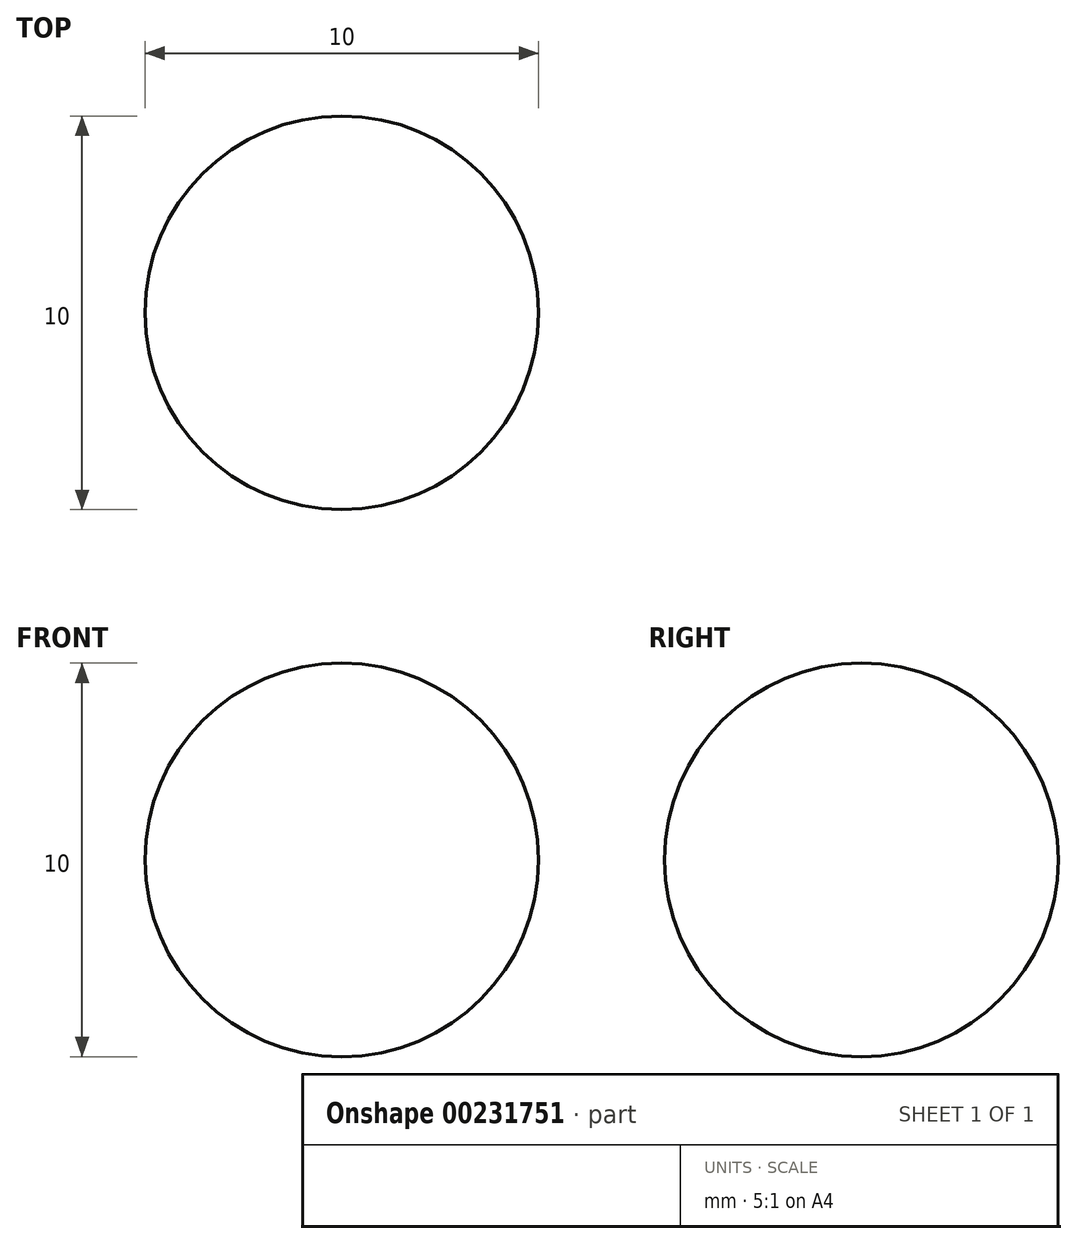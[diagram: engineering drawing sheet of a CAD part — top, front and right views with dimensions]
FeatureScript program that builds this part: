
annotation { "Feature Type Name" : "Feature", "Feature Type Description" : "" }
export const myFeature = defineFeature(function(context is Context, id is Id, definition is map)
    precondition{}
    {
        {
            var Q0;
            Q0=qCreatedBy(makeId("Front.planeOp"),FACE);
            var sketch = newSketch(context, id + "F0", { "sketchPlane" : qUnion([Q0])});
            skCircle(sketch, "E0", {"center": v(0, 0) * mm, "radius": 5 * mm});
            skLineSegment(sketch, "E1", {"start": v(0, 5) * mm, "end": v(0, -5) * mm});
            skSolve(sketch);
        }
        {
            var Q0;
            {var subQ0=sQuery(id+"F0.wireOp",EDGE,"E1");Q0=makeQuery(id+"F0.imprint","IMPRINT",FACE,{"disambiguationData":[TD([[makeQuery(id+"F0.imprint","IMPRINT",EDGE,{"derivedFrom":subQ0}),1.0]])]});}
            var Q1;
            Q1=sQuery(id+"F0.wireOp",EDGE,"E1");
            revolve(context, id + "F1", {"entities" : qUnion([Q0]), "axis" : qUnion([Q1]), "revolveType" : RevolveType.FULL});
        }
    });
